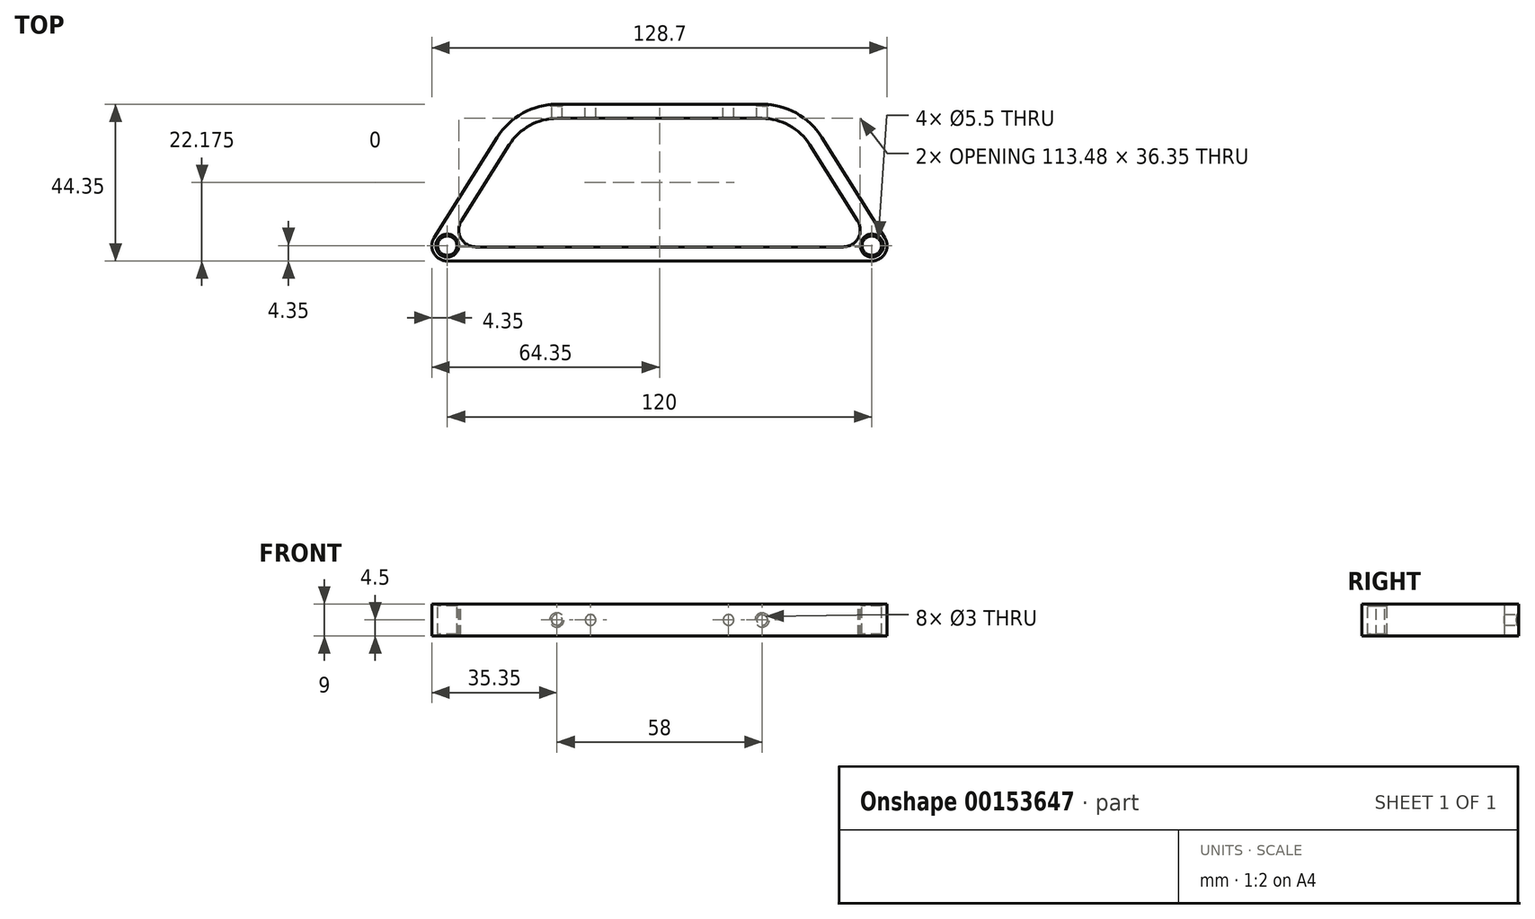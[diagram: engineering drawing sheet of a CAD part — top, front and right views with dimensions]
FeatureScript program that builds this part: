
annotation { "Feature Type Name" : "Feature", "Feature Type Description" : "" }
export const myFeature = defineFeature(function(context is Context, id is Id, definition is map)
    precondition{}
    {
        {
            var Q0;
            Q0=qCreatedBy(makeId("Top.planeOp"),FACE);
            var sketch = newSketch(context, id + "F0", { "sketchPlane" : qUnion([Q0])});
            skCircle(sketch, "E0", {"center": v(120, 0) * mm, "radius": 2.75 * mm});
            skCircle(sketch, "E1", {"center": v(0, 0) * mm, "radius": 2.75 * mm});
            skCircle(sketch, "E2", {"center": v(120, 0) * mm, "radius": 4.35 * mm});
            skCircle(sketch, "E3", {"center": v(0, 0) * mm, "radius": 4.35 * mm});
            skLineSegment(sketch, "E4", {"start": v(0, -4.35) * mm, "end": v(120, -4.35) * mm});
            skLineSegment(sketch, "E5", {"start": v(-3.68, 2.31) * mm, "end": v(14.12, 30.64) * mm});
            skLineSegment(sketch, "E6", {"start": v(31.05, 40) * mm, "end": v(88.95, 40) * mm});
            skLineSegment(sketch, "E7", {"start": v(105.88, 30.64) * mm, "end": v(123.68, 2.31) * mm});
            skPoint(sketch, "E8.visualSharp", {"position": v(20, 40) * mm});
            skArc(sketch, "E9.filletArc", {"start": v(31.05, 40) * mm, "mid": v(21.38, 37.5) * mm, "end": v(14.12, 30.64) * mm});
            skPoint(sketch, "E10.visualSharp", {"position": v(100, 40) * mm});
            skArc(sketch, "E10.filletArc", {"start": v(105.88, 30.64) * mm, "mid": v(98.62, 37.5) * mm, "end": v(88.95, 40) * mm});
            skLineSegment(sketch, "E11.0", {"start": v(102.5, 28.51) * mm, "end": v(117.99, 3.86) * mm});
            skLineSegment(sketch, "E11.1", {"start": v(2.01, 3.86) * mm, "end": v(17.5, 28.51) * mm});
            skArc(sketch, "E11.2", {"start": v(31.05, 36) * mm, "mid": v(23.31, 34) * mm, "end": v(17.5, 28.51) * mm});
            skLineSegment(sketch, "E11.3", {"start": v(31.05, 36) * mm, "end": v(88.95, 36) * mm});
            skArc(sketch, "E11.4", {"start": v(102.5, 28.51) * mm, "mid": v(96.69, 34) * mm, "end": v(88.95, 36) * mm});
            skLineSegment(sketch, "E12", {"start": v(4.34, -0.35) * mm, "end": v(115.66, -0.35) * mm});
            skSolve(sketch);
        }
        {
            var Q0;
            Q0 = qSketchRegion(id + "F0", true);
            extrude(context, id + "F1", {"entities" : qUnion([Q0]), "depth" : 9 * mm, "symmetric" : true});
        }
        {
            var Q0;
            Q0 = qSketchRegion(id + "F0", true);
            extrude(context, id + "F2", {"entities" : qUnion([Q0]), "oppositeDirection" : true, "depth" : 9 * mm, "symmetric" : true});
        }
        {
            var Q0;
            Q0=makeQuery(id+"F1.opExtrude","SWEPT_EDGE",EDGE,{"disambiguationData":[OSD([sQuery(id+"F0.wireOp",EDGE,"E3"),sQuery(id+"F0.wireOp",EDGE,"E11.1")])]});
            var Q1;
            Q1=makeQuery(id+"F1.opExtrude","SWEPT_EDGE",EDGE,{"disambiguationData":[OSD([sQuery(id+"F0.wireOp",EDGE,"E3"),sQuery(id+"F0.wireOp",EDGE,"E12")])]});
            var Q2;
            Q2=makeQuery(id+"F1.opExtrude","SWEPT_EDGE",EDGE,{"disambiguationData":[OSD([sQuery(id+"F0.wireOp",EDGE,"E2"),sQuery(id+"F0.wireOp",EDGE,"E12")])]});
            var Q3;
            Q3=makeQuery(id+"F1.opExtrude","SWEPT_EDGE",EDGE,{"disambiguationData":[OSD([sQuery(id+"F0.wireOp",EDGE,"E2"),sQuery(id+"F0.wireOp",EDGE,"E11.0")])]});
            var Q4;
            Q4=makeQuery(id+"F2.opExtrude","SWEPT_EDGE",EDGE,{"disambiguationData":[OSD([sQuery(id+"F0.wireOp",EDGE,"E2"),sQuery(id+"F0.wireOp",EDGE,"E11.0")])]});
            var Q5;
            Q5=makeQuery(id+"F2.opExtrude","SWEPT_EDGE",EDGE,{"disambiguationData":[OSD([sQuery(id+"F0.wireOp",EDGE,"E2"),sQuery(id+"F0.wireOp",EDGE,"E12")])]});
            var Q6;
            Q6=makeQuery(id+"F2.opExtrude","SWEPT_EDGE",EDGE,{"disambiguationData":[OSD([sQuery(id+"F0.wireOp",EDGE,"E3"),sQuery(id+"F0.wireOp",EDGE,"E11.1")])]});
            var Q7;
            Q7=makeQuery(id+"F2.opExtrude","SWEPT_EDGE",EDGE,{"disambiguationData":[OSD([sQuery(id+"F0.wireOp",EDGE,"E3"),sQuery(id+"F0.wireOp",EDGE,"E12")])]});
            fillet(context, id + "F3", {"entities" : qUnion([Q0, Q1, Q2, Q3, Q4, Q5, Q6, Q7]), "radius" : 5 * mm, "tangentPropagation" : true, "allowEdgeOverflow" : false});
        }
        {
            var Q0;
            Q0=makeQuery(id+"F1.opExtrude","SWEPT_FACE",FACE,{"disambiguationData":[OSD([sQuery(id+"F0.wireOp",EDGE,"E6")])]});
            var sketch = newSketch(context, id + "F4", { "sketchPlane" : qUnion([Q0])});
            skCircle(sketch, "E13", {"center": v(-40.5, 0) * mm, "radius": 1.5 * mm});
            skCircle(sketch, "E14", {"center": v(-79.5, 0) * mm, "radius": 1.5 * mm});
            skLineSegment(sketch, "E15", {"start": v(-31.05, 0) * mm, "end": v(-88.95, 0) * mm, "construction": true});
            skPoint(sketch, "E16", {"position": v(-60, 0) * mm});
            skCircle(sketch, "E17", {"center": v(-31, 0) * mm, "radius": 1.5 * mm});
            skCircle(sketch, "E18", {"center": v(-89, 0) * mm, "radius": 1.5 * mm});
            skSolve(sketch);
        }
        {
            var Q0;
            Q0=makeQuery(id+"F4.imprint","IMPRINT",FACE,{"disambiguationData":[TD([[makeQuery(id+"F4.imprint","IMPRINT",EDGE,{"derivedFrom":sQuery(id+"F4.wireOp",EDGE,"E13")}),1.0]])]});
            var Q1;
            Q1=makeQuery(id+"F4.imprint","IMPRINT",FACE,{"disambiguationData":[TD([[makeQuery(id+"F4.imprint","IMPRINT",EDGE,{"derivedFrom":sQuery(id+"F4.wireOp",EDGE,"E14")}),1.0]])]});
            extrude(context, id + "F5", {"entities" : qUnion([Q0, Q1]), "operationType" : NewBodyOperationType.REMOVE, "oppositeDirection" : true, "depth" : 5 * mm});
        }
        {
            var Q0;
            {var subQ0=sQuery(id+"F4.wireOp",EDGE,"E17");var subQ1=makeQuery(id+"F1.opExtrude","SWEPT_EDGE",EDGE,{"disambiguationData":[OSD([sQuery(id+"F0.wireOp",EDGE,"E6"),sQuery(id+"F0.wireOp",EDGE,"E9.filletArc")])]});var subQ2=makeQuery(id+"F4.imprint","INTERSECT",VERTEX,{"disambiguationData":[OD(0.0)],"derivedFrom":[subQ1,subQ0]});Q0=makeQuery(id+"F4.imprint","IMPRINT",FACE,{"disambiguationData":[TD([[makeQuery(id+"F4.imprint","IMPRINT",EDGE,{"disambiguationData":[TD([[subQ2,-1.0]])],"derivedFrom":subQ0}),1.0]])]});}
            var Q1;
            {var subQ0=sQuery(id+"F4.wireOp",EDGE,"E18");var subQ1=makeQuery(id+"F1.opExtrude","SWEPT_EDGE",EDGE,{"disambiguationData":[OSD([sQuery(id+"F0.wireOp",EDGE,"E6"),sQuery(id+"F0.wireOp",EDGE,"E10.filletArc")])]});var subQ2=makeQuery(id+"F4.imprint","INTERSECT",VERTEX,{"disambiguationData":[OD(0.0)],"derivedFrom":[subQ1,subQ0]});Q1=makeQuery(id+"F4.imprint","IMPRINT",FACE,{"disambiguationData":[TD([[makeQuery(id+"F4.imprint","IMPRINT",EDGE,{"disambiguationData":[TD([[subQ2,1.0]])],"derivedFrom":subQ0}),1.0]])]});}
            var Q2;
            {var subQ0=sQuery(id+"F4.wireOp",EDGE,"E17");var subQ1=makeQuery(id+"F1.opExtrude","SWEPT_EDGE",EDGE,{"disambiguationData":[OSD([sQuery(id+"F0.wireOp",EDGE,"E6"),sQuery(id+"F0.wireOp",EDGE,"E9.filletArc")])]});var subQ2=makeQuery(id+"F4.imprint","INTERSECT",VERTEX,{"disambiguationData":[OD(0.0)],"derivedFrom":[subQ1,subQ0]});Q2=makeQuery(id+"F4.imprint","IMPRINT",FACE,{"disambiguationData":[TD([[makeQuery(id+"F4.imprint","IMPRINT",EDGE,{"disambiguationData":[TD([[subQ2,1.0]])],"derivedFrom":subQ0}),1.0]])]});}
            var Q3;
            {var subQ0=sQuery(id+"F4.wireOp",EDGE,"E18");var subQ1=makeQuery(id+"F1.opExtrude","SWEPT_EDGE",EDGE,{"disambiguationData":[OSD([sQuery(id+"F0.wireOp",EDGE,"E6"),sQuery(id+"F0.wireOp",EDGE,"E10.filletArc")])]});var subQ2=makeQuery(id+"F4.imprint","INTERSECT",VERTEX,{"disambiguationData":[OD(0.0)],"derivedFrom":[subQ1,subQ0]});Q3=makeQuery(id+"F4.imprint","IMPRINT",FACE,{"disambiguationData":[TD([[makeQuery(id+"F4.imprint","IMPRINT",EDGE,{"disambiguationData":[TD([[subQ2,-1.0]])],"derivedFrom":subQ0}),1.0]])]});}
            extrude(context, id + "F6", {"entities" : qUnion([Q0, Q1, Q2, Q3]), "operationType" : NewBodyOperationType.REMOVE, "oppositeDirection" : true, "depth" : 5 * mm});
        }
        {
            var Q0;
            {var subQ0=sQuery(id+"F4.wireOp",EDGE,"E14");Q0=makeQuery(id+"F5.boolean.opBoolean","COPY",EDGE,{"disambiguationData":[TD([makeQuery(id+"F1.opExtrude","SWEPT_FACE",FACE,{"disambiguationData":[OSD([sQuery(id+"F0.wireOp",EDGE,"E6")])]})])],"derivedFrom":makeQuery(id+"F5.opExtrude","CAP_EDGE",EDGE,{"disambiguationData":[OSD([subQ0])],"isStart":true})});}
            var Q1;
            Q1=makeQuery(id+"F1.opExtrude","CAP_EDGE",EDGE,{"disambiguationData":[OSD([sQuery(id+"F0.wireOp",EDGE,"E1")])],"isStart":false});
            var Q2;
            Q2=makeQuery(id+"F1.opExtrude","CAP_EDGE",EDGE,{"disambiguationData":[OSD([sQuery(id+"F0.wireOp",EDGE,"E1")])],"isStart":true});
            var Q3;
            Q3=makeQuery(id+"F1.opExtrude","CAP_EDGE",EDGE,{"disambiguationData":[OSD([sQuery(id+"F0.wireOp",EDGE,"E0")])],"isStart":false});
            var Q4;
            Q4=makeQuery(id+"F1.opExtrude","CAP_EDGE",EDGE,{"disambiguationData":[OSD([sQuery(id+"F0.wireOp",EDGE,"E0")])],"isStart":true});
            var Q5;
            {var subQ0=sQuery(id+"F4.wireOp",EDGE,"E13");Q5=makeQuery(id+"F5.boolean.opBoolean","COPY",EDGE,{"disambiguationData":[TD([makeQuery(id+"F1.opExtrude","SWEPT_FACE",FACE,{"disambiguationData":[OSD([sQuery(id+"F0.wireOp",EDGE,"E6")])]})])],"derivedFrom":makeQuery(id+"F5.opExtrude","CAP_EDGE",EDGE,{"disambiguationData":[OSD([subQ0])],"isStart":true})});}
            var Q6;
            Q6=makeQuery(id+"F2.opExtrude","CAP_EDGE",EDGE,{"disambiguationData":[OSD([sQuery(id+"F0.wireOp",EDGE,"E0")])],"isStart":true});
            var Q7;
            Q7=makeQuery(id+"F2.opExtrude","CAP_EDGE",EDGE,{"disambiguationData":[OSD([sQuery(id+"F0.wireOp",EDGE,"E0")])],"isStart":false});
            var Q8;
            Q8=makeQuery(id+"F2.opExtrude","CAP_EDGE",EDGE,{"disambiguationData":[OSD([sQuery(id+"F0.wireOp",EDGE,"E1")])],"isStart":false});
            var Q9;
            Q9=makeQuery(id+"F2.opExtrude","CAP_EDGE",EDGE,{"disambiguationData":[OSD([sQuery(id+"F0.wireOp",EDGE,"E1")])],"isStart":true});
            var Q10;
            {var subQ0=sQuery(id+"F4.wireOp",EDGE,"E13");Q10=makeQuery(id+"F5.boolean.opBoolean","COPY",EDGE,{"disambiguationData":[TD([makeQuery(id+"F2.opExtrude","SWEPT_FACE",FACE,{"disambiguationData":[OSD([sQuery(id+"F0.wireOp",EDGE,"E6")])]})])],"derivedFrom":makeQuery(id+"F5.opExtrude","CAP_EDGE",EDGE,{"disambiguationData":[OSD([subQ0])],"isStart":true})});}
            var Q11;
            {var subQ0=sQuery(id+"F4.wireOp",EDGE,"E14");Q11=makeQuery(id+"F5.boolean.opBoolean","COPY",EDGE,{"disambiguationData":[TD([makeQuery(id+"F2.opExtrude","SWEPT_FACE",FACE,{"disambiguationData":[OSD([sQuery(id+"F0.wireOp",EDGE,"E6")])]})])],"derivedFrom":makeQuery(id+"F5.opExtrude","CAP_EDGE",EDGE,{"disambiguationData":[OSD([subQ0])],"isStart":true})});}
            var Q12;
            Q12=makeQuery(id+"F6.boolean.opBoolean","INTERSECT",EDGE,{"derivedFrom":[makeQuery(id+"F2.opExtrude","SWEPT_FACE",FACE,{"disambiguationData":[OSD([sQuery(id+"F0.wireOp",EDGE,"E10.filletArc")])]}),makeQuery(id+"F6.opExtrude","SWEPT_FACE",FACE,{"disambiguationData":[OSD([sQuery(id+"F4.wireOp",EDGE,"E18")])]})]});
            var Q13;
            Q13=makeQuery(id+"F6.boolean.opBoolean","COPY",EDGE,{"derivedFrom":makeQuery(id+"F6.opExtrude","CAP_EDGE",EDGE,{"disambiguationData":[OSD([sQuery(id+"F4.wireOp",EDGE,"E18")])],"isStart":true})});
            var Q14;
            Q14=makeQuery(id+"F6.boolean.opBoolean","COPY",EDGE,{"derivedFrom":makeQuery(id+"F6.opExtrude","CAP_EDGE",EDGE,{"disambiguationData":[OSD([sQuery(id+"F4.wireOp",EDGE,"E17")])],"isStart":true})});
            var Q15;
            Q15=makeQuery(id+"F6.boolean.opBoolean","INTERSECT",EDGE,{"derivedFrom":[makeQuery(id+"F2.opExtrude","SWEPT_FACE",FACE,{"disambiguationData":[OSD([sQuery(id+"F0.wireOp",EDGE,"E9.filletArc")])]}),makeQuery(id+"F6.opExtrude","SWEPT_FACE",FACE,{"disambiguationData":[OSD([sQuery(id+"F4.wireOp",EDGE,"E17")])]})]});
            chamfer(context, id + "F7", {"entities" : qUnion([Q0, Q1, Q2, Q3, Q4, Q5, Q6, Q7, Q8, Q9, Q10, Q11, Q12, Q13, Q14, Q15]), "width" : .5 * mm, "tangentPropagation" : true});
        }
    });
